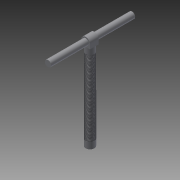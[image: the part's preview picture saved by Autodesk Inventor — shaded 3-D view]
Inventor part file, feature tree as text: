
AUTODESK INVENTOR PART (.ipt)
format: ipt  version: 2015 (Build 190159000, 159)  size: 104,448 bytes
history: native  units: in
note: dims shown in document units (in); Inventor stores cm internally (conversion verified against a paired STEP export)
features: extrude x4, sketch x4, fillet x1, thread x1
ambient origin geometry x8: Origin, YZ Plane, XZ Plane, XY Plane, X Axis, Y Axis, Z Axis, Center Point
bodies: Solid1 (feature_tree)
feature tree (10):
  extrude  "Extrusion1"  Depth=27.5591in TaperAngle=0.0deg
  extrude  "Extrusion2"  Depth=1.378in
  extrude  "Extrusion3"  Depth=2.7559in
  extrude  "Extrusion4"  Depth=2.7559in TaperAngle=0.0deg
  fillet  "Fillet1"  Radius=1.9685in
  thread  "Thread1"  [1 undecoded]
  sketch  "Sketch1"  dims[d0=2.7559in d1=27.5591in d2=0.0in]
  sketch  "Sketch2"  dims[d3=1.378in d4=1.378in]
  sketch  "Sketch3"  dims[d5=2.7559in d6=2.7559in]
  sketch  "Sketch4"  dims[d7=2.7559in d8=2.7559in d9=0.0in d10=1.9685in d11=11.811in d12=0.0in d13=1.378in d14=1.378in d15=1.9685in d16=11.811in d17=0.0in d18=1.378in d19=23.622in d20=1.9685in]
note: 1 required parameter value undecoded (feature->parameter linkage not recoverable at this tier; creation-order binding heuristic only, values carry confidence <= 0.55)
